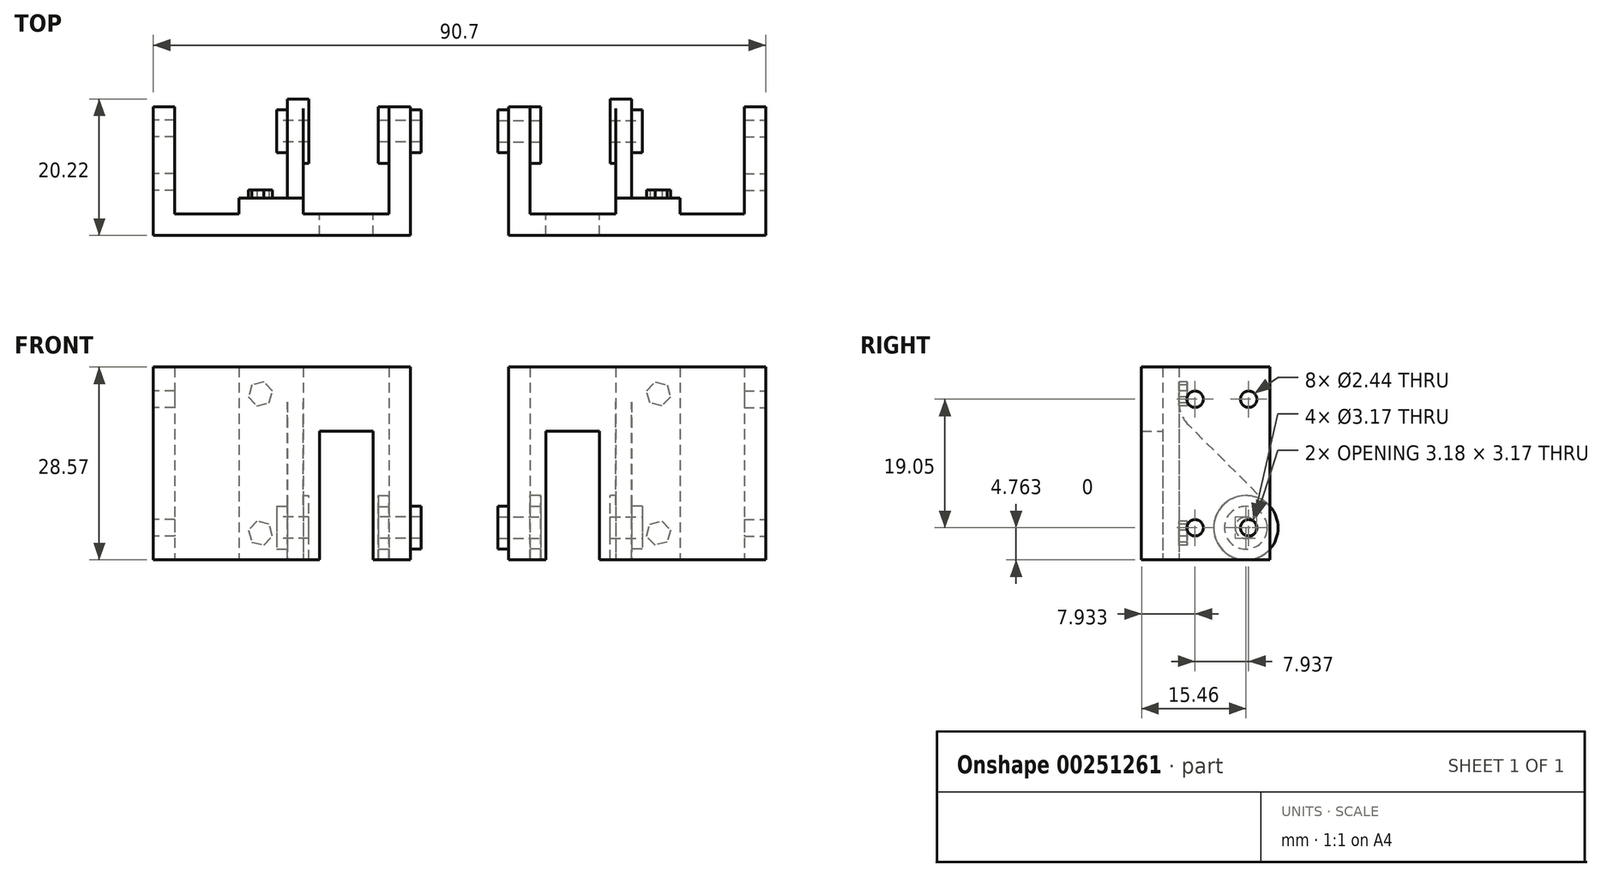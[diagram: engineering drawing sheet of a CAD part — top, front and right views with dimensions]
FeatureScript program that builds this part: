
annotation { "Feature Type Name" : "Feature", "Feature Type Description" : "" }
export const myFeature = defineFeature(function(context is Context, id is Id, definition is map)
    precondition{}
    {
        {
            var Q0;
            Q0=qCreatedBy(makeId("Front.planeOp"),FACE);
            var sketch = newSketch(context, id + "F0", { "sketchPlane" : qUnion([Q0])});
            skLineSegment(sketch, "E0", {"start": v(-7.25, 0) * mm, "end": v(-12.81, 0) * mm});
            skLineSegment(sketch, "E1", {"start": v(-12.81, 0) * mm, "end": v(-12.81, 19.05) * mm});
            skLineSegment(sketch, "E2", {"start": v(-12.81, 19.05) * mm, "end": v(-20.75, 19.05) * mm});
            skLineSegment(sketch, "E3", {"start": v(-20.75, 19.05) * mm, "end": v(-20.75, 0) * mm});
            skLineSegment(sketch, "E4", {"start": v(-20.75, 0) * mm, "end": v(-45.35, 0) * mm});
            skLineSegment(sketch, "E5", {"start": v(-45.35, 0) * mm, "end": v(-45.35, 28.58) * mm});
            skLineSegment(sketch, "E6", {"start": v(-45.35, 28.58) * mm, "end": v(-7.25, 28.58) * mm});
            skLineSegment(sketch, "E7", {"start": v(-7.25, 28.58) * mm, "end": v(-7.25, 0) * mm});
            skSolve(sketch);
        }
        {
            var Q0;
            Q0 = qSketchRegion(id + "F0", true);
            extrude(context, id + "F1", {"entities" : qUnion([Q0]), "depth" : 3.17 * mm});
        }
        {
            var Q0;
            Q0=makeQuery(id+"F1.opExtrude","CAP_FACE",FACE,{"disambiguationData":[OSD([sQuery(id+"F0.wireOp",EDGE,"E0"),sQuery(id+"F0.wireOp",EDGE,"E1"),sQuery(id+"F0.wireOp",EDGE,"E2"),sQuery(id+"F0.wireOp",EDGE,"E3"),sQuery(id+"F0.wireOp",EDGE,"E4"),sQuery(id+"F0.wireOp",EDGE,"E5"),sQuery(id+"F0.wireOp",EDGE,"E6"),sQuery(id+"F0.wireOp",EDGE,"E7")])],"isStart":true});
            var sketch = newSketch(context, id + "F2", { "sketchPlane" : qUnion([Q0])});
            skLineSegment(sketch, "E8", {"start": v(10.43, 28.58) * mm, "end": v(10.43, 0) * mm});
            skLineSegment(sketch, "E9", {"start": v(42.18, 28.58) * mm, "end": v(42.18, 0) * mm});
            skSolve(sketch);
        }
        {
            var Q0;
            {var subQ0=sQuery(id+"F2.wireOp",EDGE,"E9");Q0=makeQuery(id+"F2.imprint","IMPRINT",FACE,{"disambiguationData":[TD([[makeQuery(id+"F2.imprint","IMPRINT",EDGE,{"derivedFrom":subQ0}),1.0]])]});}
            extrude(context, id + "F3", {"entities" : qUnion([Q0]), "operationType" : NewBodyOperationType.ADD, "depth" : 15.88 * mm});
        }
        {
            var Q0;
            Q0=makeQuery(id+"F1.opExtrude","CAP_FACE",FACE,{"disambiguationData":[OSD([sQuery(id+"F0.wireOp",EDGE,"E0"),sQuery(id+"F0.wireOp",EDGE,"E1"),sQuery(id+"F0.wireOp",EDGE,"E2"),sQuery(id+"F0.wireOp",EDGE,"E3"),sQuery(id+"F0.wireOp",EDGE,"E4"),sQuery(id+"F0.wireOp",EDGE,"E5"),sQuery(id+"F0.wireOp",EDGE,"E6"),sQuery(id+"F0.wireOp",EDGE,"E7")])],"isStart":true});
            var sketch = newSketch(context, id + "F4", { "sketchPlane" : qUnion([Q0])});
            skLineSegment(sketch, "E10", {"start": v(10.43, 28.58) * mm, "end": v(10.43, 0) * mm});
            skSolve(sketch);
        }
        {
            var Q0;
            Q0 = qSketchRegion(id + "F4", true);
            var Q1;
            {var subQ0=sQuery(id+"F4.wireOp",EDGE,"E10");Q1=makeQuery(id+"F4.imprint","IMPRINT",FACE,{"disambiguationData":[TD([[makeQuery(id+"F4.imprint","IMPRINT",EDGE,{"derivedFrom":subQ0}),-1.0]])]});}
            extrude(context, id + "F5", {"entities" : qUnion([Q0, Q1]), "operationType" : NewBodyOperationType.ADD, "depth" : 15.88 * mm});
        }
        {
            var Q0;
            Q0=makeQuery(id+"F1.opExtrude","CAP_FACE",FACE,{"disambiguationData":[OSD([sQuery(id+"F0.wireOp",EDGE,"E0"),sQuery(id+"F0.wireOp",EDGE,"E1"),sQuery(id+"F0.wireOp",EDGE,"E2"),sQuery(id+"F0.wireOp",EDGE,"E3"),sQuery(id+"F0.wireOp",EDGE,"E4"),sQuery(id+"F0.wireOp",EDGE,"E5"),sQuery(id+"F0.wireOp",EDGE,"E6"),sQuery(id+"F0.wireOp",EDGE,"E7")])],"isStart":true});
            var sketch = newSketch(context, id + "F6", { "sketchPlane" : qUnion([Q0])});
            skLineSegment(sketch, "E11", {"start": v(23.13, 28.58) * mm, "end": v(23.13, 0) * mm});
            skLineSegment(sketch, "E12", {"start": v(32.65, 28.58) * mm, "end": v(32.65, 0) * mm});
            skSolve(sketch);
        }
        {
            var Q0;
            {var subQ0=sQuery(id+"F6.wireOp",EDGE,"E11");Q0=makeQuery(id+"F6.imprint","IMPRINT",FACE,{"disambiguationData":[TD([[makeQuery(id+"F6.imprint","IMPRINT",EDGE,{"derivedFrom":subQ0}),1.0]])]});}
            extrude(context, id + "F7", {"entities" : qUnion([Q0]), "operationType" : NewBodyOperationType.ADD, "depth" : 2.38 * mm});
        }
        {
            var Q0;
            Q0=makeQuery(id+"F7.opExtrude","CAP_FACE",FACE,{"disambiguationData":[OSD([sQuery(id+"F0.wireOp",EDGE,"E4"),sQuery(id+"F0.wireOp",EDGE,"E6"),sQuery(id+"F6.wireOp",EDGE,"E11"),sQuery(id+"F6.wireOp",EDGE,"E12")])],"isStart":false});
            var sketch = newSketch(context, id + "F8", { "sketchPlane" : qUnion([Q0])});
            skLineSegment(sketch, "E13", {"start": v(25.51, 28.58) * mm, "end": v(25.51, 0) * mm});
            skSolve(sketch);
        }
        {
            var Q0;
            Q0 = qSketchRegion(id + "F8", true);
            var Q1;
            {var subQ0=sQuery(id+"F8.wireOp",EDGE,"E13");Q1=makeQuery(id+"F8.imprint","IMPRINT",FACE,{"disambiguationData":[TD([[makeQuery(id+"F8.imprint","IMPRINT",EDGE,{"derivedFrom":subQ0}),-1.0]])]});}
            extrude(context, id + "F9", {"entities" : qUnion([Q0, Q1]), "operationType" : NewBodyOperationType.ADD, "depth" : 15.08 * mm});
        }
        {
            var Q0;
            {var subQ0=sQuery(id+"F6.wireOp",EDGE,"E11");Q0=makeQuery(id+"F9.boolean.opBoolean","MERGE",FACE,{"derivedFrom":[makeQuery(id+"F7.opExtrude","SWEPT_FACE",FACE,{"disambiguationData":[OSD([subQ0])]}),makeQuery(id+"F9.opExtrude","SWEPT_FACE",FACE,{"disambiguationData":[OSD([subQ0])]})]});}
            var sketch = newSketch(context, id + "F10", { "sketchPlane" : qUnion([Q0])});
            skCircle(sketch, "E14", {"center": v(12.3, 4.76) * mm, "radius": 4.76 * mm});
            skLineSegment(sketch, "E15", {"start": v(2.38, 28.58) * mm, "end": v(2.38, 11.63) * mm});
            skLineSegment(sketch, "E16", {"start": v(15.66, 8.13) * mm, "end": v(2.38, 21.4) * mm});
            skSolve(sketch);
        }
        {
            var Q0;
            {var subQ5=sQuery(id+"F10.wireOp",EDGE,"E16");Q0=makeQuery(id+"F10.imprint","IMPRINT",FACE,{"disambiguationData":[TD([[makeQuery(id+"F10.imprint","IMPRINT",EDGE,{"derivedFrom":subQ5}),-1.0]])]});}
            extrude(context, id + "F11", {"entities" : qUnion([Q0]), "operationType" : NewBodyOperationType.REMOVE, "oppositeDirection" : true, "depth" : 2.38 * mm});
        }
        {
            var Q0;
            Q0=makeQuery(id+"F11.boolean.opBoolean","COPY",EDGE,{"derivedFrom":makeQuery(id+"F11.opExtrude","SWEPT_EDGE",EDGE,{"disambiguationData":[OSD([sQuery(id+"F10.wireOp",EDGE,"E15"),sQuery(id+"F10.wireOp",EDGE,"E16")])]})});
            fillet(context, id + "F12", {"entities" : qUnion([Q0]), "radius" : 4.76 * mm, "tangentPropagation" : true, "allowEdgeOverflow" : false});
        }
        {
            var Q0;
            {var subQ0=sQuery(id+"F6.wireOp",EDGE,"E11");Q0=makeQuery(id+"F9.boolean.opBoolean","MERGE",FACE,{"derivedFrom":[makeQuery(id+"F7.opExtrude","SWEPT_FACE",FACE,{"disambiguationData":[OSD([subQ0])]}),makeQuery(id+"F9.opExtrude","SWEPT_FACE",FACE,{"disambiguationData":[OSD([subQ0])]})]});}
            var sketch = newSketch(context, id + "F13", { "sketchPlane" : qUnion([Q0])});
            skCircle(sketch, "E17", {"center": v(12.3, 4.76) * mm, "radius": 4.76 * mm});
            skSolve(sketch);
        }
        {
            var Q0;
            Q0 = qSketchRegion(id + "F13", true);
            extrude(context, id + "F14", {"entities" : qUnion([Q0]), "operationType" : NewBodyOperationType.ADD, "depth" : 0.8 * mm});
        }
        {
            var Q0;
            Q0=makeQuery(id+"F9.opExtrude","SWEPT_FACE",FACE,{"disambiguationData":[OSD([sQuery(id+"F8.wireOp",EDGE,"E13")])]});
            var sketch = newSketch(context, id + "F15", { "sketchPlane" : qUnion([Q0])});
            skCircle(sketch, "E18", {"center": v(-12.3, 4.76) * mm, "radius": 3.17 * mm});
            skSolve(sketch);
        }
        {
            var Q0;
            Q0 = qSketchRegion(id + "F15", true);
            extrude(context, id + "F16", {"entities" : qUnion([Q0]), "operationType" : NewBodyOperationType.ADD, "depth" : 1.59 * mm});
        }
        {
            var Q0;
            Q0=makeQuery(id+"F16.opExtrude","CAP_FACE",FACE,{"disambiguationData":[OSD([sQuery(id+"F15.wireOp",EDGE,"E18")])],"isStart":false});
            var sketch = newSketch(context, id + "F17", { "sketchPlane" : qUnion([Q0])});
            skCircle(sketch, "E19", {"center": v(-12.3, 4.76) * mm, "radius": 1.59 * mm});
            skSolve(sketch);
        }
        {
            var Q0;
            Q0 = qSketchRegion(id + "F17", true);
            extrude(context, id + "F18", {"entities" : qUnion([Q0]), "operationType" : NewBodyOperationType.REMOVE, "oppositeDirection" : true, "depth" : 25.4 * mm});
        }
        {
            var Q0;
            Q0=makeQuery(id+"F5.opExtrude","SWEPT_FACE",FACE,{"disambiguationData":[OSD([sQuery(id+"F4.wireOp",EDGE,"E10")])]});
            var sketch = newSketch(context, id + "F19", { "sketchPlane" : qUnion([Q0])});
            skCircle(sketch, "E20", {"center": v(-12.3, 4.76) * mm, "radius": 4.76 * mm});
            skSolve(sketch);
        }
        {
            var Q0;
            {var subQ1=sQuery(id+"F4.wireOp",EDGE,"E10");Q0=makeQuery(id+"F19.imprint","IMPRINT",FACE,{"disambiguationData":[TD([[makeQuery(id+"F19.imprint","IMPRINT",EDGE,{"derivedFrom":makeQuery(id+"F18.boolean.opBoolean","INTERSECT",EDGE,{"derivedFrom":[makeQuery(id+"F5.opExtrude","SWEPT_FACE",FACE,{"disambiguationData":[OSD([subQ1])]}),makeQuery(id+"F18.opExtrude","SWEPT_FACE",FACE,{"disambiguationData":[OSD([sQuery(id+"F17.wireOp",EDGE,"E19")])]})]})}),-1.0]])]});}
            var Q1;
            {var subQ0=sQuery(id+"F19.wireOp",EDGE,"E20");var subQ1=makeQuery(id+"F5.opExtrude","CAP_EDGE",EDGE,{"disambiguationData":[OSD([sQuery(id+"F4.wireOp",EDGE,"E10")])],"isStart":false});var subQ2=makeQuery(id+"F19.imprint","INTERSECT",VERTEX,{"disambiguationData":[OD(0.0)],"derivedFrom":[subQ1,subQ0]});Q1=makeQuery(id+"F19.imprint","IMPRINT",FACE,{"disambiguationData":[TD([[makeQuery(id+"F19.imprint","IMPRINT",EDGE,{"disambiguationData":[TD([[subQ2,1.0]])],"derivedFrom":subQ0}),1.0]])]});}
            extrude(context, id + "F20", {"entities" : qUnion([Q0, Q1]), "operationType" : NewBodyOperationType.ADD, "depth" : 1.59 * mm});
        }
        {
            var Q0;
            {var subQ0=sQuery(id+"F0.wireOp",EDGE,"E7");Q0=makeQuery(id+"F5.boolean.opBoolean","MERGE",FACE,{"derivedFrom":[makeQuery(id+"F1.opExtrude","SWEPT_FACE",FACE,{"disambiguationData":[OSD([subQ0])]}),makeQuery(id+"F5.opExtrude","SWEPT_FACE",FACE,{"disambiguationData":[OSD([subQ0])]})]});}
            var sketch = newSketch(context, id + "F21", { "sketchPlane" : qUnion([Q0])});
            skCircle(sketch, "E21", {"center": v(12.3, 4.76) * mm, "radius": 3.18 * mm});
            skSolve(sketch);
        }
        {
            var Q0;
            Q0=makeQuery(id+"F21.imprint","IMPRINT",FACE,{"disambiguationData":[TD([[makeQuery(id+"F21.imprint","IMPRINT",EDGE,{"derivedFrom":sQuery(id+"F21.wireOp",EDGE,"E21")}),1.0]])]});
            extrude(context, id + "F22", {"entities" : qUnion([Q0]), "operationType" : NewBodyOperationType.ADD, "depth" : 1.59 * mm});
        }
        {
            var Q0;
            {var subQ0=sQuery(id+"F0.wireOp",EDGE,"E5");Q0=makeQuery(id+"F3.boolean.opBoolean","MERGE",FACE,{"derivedFrom":[makeQuery(id+"F1.opExtrude","SWEPT_FACE",FACE,{"disambiguationData":[OSD([subQ0])]}),makeQuery(id+"F3.opExtrude","SWEPT_FACE",FACE,{"disambiguationData":[OSD([subQ0])]})]});}
            var sketch = newSketch(context, id + "F23", { "sketchPlane" : qUnion([Q0])});
            skCircle(sketch, "E22", {"center": v(-12.7, 23.81) * mm, "radius": 1.22 * mm});
            skCircle(sketch, "E23", {"center": v(-4.76, 23.81) * mm, "radius": 1.22 * mm});
            skCircle(sketch, "E24", {"center": v(-12.7, 4.76) * mm, "radius": 1.22 * mm});
            skCircle(sketch, "E25", {"center": v(-4.76, 4.76) * mm, "radius": 1.22 * mm});
            skSolve(sketch);
        }
        {
            var Q0;
            Q0 = qSketchRegion(id + "F23", true);
            extrude(context, id + "F24", {"entities" : qUnion([Q0]), "operationType" : NewBodyOperationType.REMOVE, "oppositeDirection" : true, "depth" : 4.76 * mm});
        }
        {
            var Q0;
            Q0=makeQuery(id+"F11.boolean.opBoolean","MERGE",FACE,{"derivedFrom":[makeQuery(id+"F7.opExtrude","CAP_FACE",FACE,{"disambiguationData":[OSD([sQuery(id+"F0.wireOp",EDGE,"E4"),sQuery(id+"F0.wireOp",EDGE,"E6"),sQuery(id+"F6.wireOp",EDGE,"E11"),sQuery(id+"F6.wireOp",EDGE,"E12")])],"isStart":false}),makeQuery(id+"F11.opExtrude","SWEPT_FACE",FACE,{"disambiguationData":[OSD([sQuery(id+"F10.wireOp",EDGE,"E15")])]})]});
            var sketch = newSketch(context, id + "F25", { "sketchPlane" : qUnion([Q0])});
            skCircle(sketch, "E26.cCircle", {"center": v(29.48, 24.6) * mm, "radius": 1.59 * mm, "construction": true});
            skLineSegment(sketch, "E26.0", {"start": v(31.26, 24.17) * mm, "end": v(30, 22.85) * mm});
            skLineSegment(sketch, "E26.1", {"start": v(30, 22.85) * mm, "end": v(28.21, 23.28) * mm});
            skLineSegment(sketch, "E26.2", {"start": v(28.21, 23.28) * mm, "end": v(27.7, 25.04) * mm});
            skLineSegment(sketch, "E26.3", {"start": v(27.7, 25.04) * mm, "end": v(28.97, 26.37) * mm});
            skLineSegment(sketch, "E26.4", {"start": v(28.97, 26.37) * mm, "end": v(30.75, 25.93) * mm});
            skLineSegment(sketch, "E26.5", {"start": v(30.75, 25.93) * mm, "end": v(31.26, 24.17) * mm});
            skPoint(sketch, "E26.0.midPoint", {"position": v(30.63, 23.5) * mm});
            skCircle(sketch, "E27.cCircle", {"center": v(29.48, 3.97) * mm, "radius": 1.59 * mm, "construction": true});
            skLineSegment(sketch, "E27.0", {"start": v(30.76, 2.65) * mm, "end": v(28.98, 2.2) * mm});
            skLineSegment(sketch, "E27.1", {"start": v(28.98, 2.2) * mm, "end": v(27.7, 3.52) * mm});
            skLineSegment(sketch, "E27.2", {"start": v(27.7, 3.52) * mm, "end": v(28.2, 5.28) * mm});
            skLineSegment(sketch, "E27.3", {"start": v(28.2, 5.28) * mm, "end": v(29.98, 5.73) * mm});
            skLineSegment(sketch, "E27.4", {"start": v(29.98, 5.73) * mm, "end": v(31.26, 4.42) * mm});
            skLineSegment(sketch, "E27.5", {"start": v(31.26, 4.42) * mm, "end": v(30.76, 2.65) * mm});
            skPoint(sketch, "E27.0.midPoint", {"position": v(29.87, 2.43) * mm});
            skSolve(sketch);
        }
        {
            var Q0;
            Q0 = qSketchRegion(id + "F25", true);
            extrude(context, id + "F26", {"entities" : qUnion([Q0]), "operationType" : NewBodyOperationType.ADD, "depth" : 1.2 * mm});
        }
        {
            var Q0;
            Q0=makeQuery(id+"F1.opExtrude","SWEPT_BODY",BODY,{"disambiguationData":[OSD([sQuery(id+"F0.wireOp",EDGE,"E0"),sQuery(id+"F0.wireOp",EDGE,"E1"),sQuery(id+"F0.wireOp",EDGE,"E2"),sQuery(id+"F0.wireOp",EDGE,"E3"),sQuery(id+"F0.wireOp",EDGE,"E4"),sQuery(id+"F0.wireOp",EDGE,"E5"),sQuery(id+"F0.wireOp",EDGE,"E6"),sQuery(id+"F0.wireOp",EDGE,"E7")])]});
            var Q1;
            Q1=qCreatedBy(makeId("Right.planeOp"),FACE);
            mirror(context, id + "F27", {"entities" : qUnion([Q0]), "mirrorPlane" : qUnion([Q1])});
        }
    });
